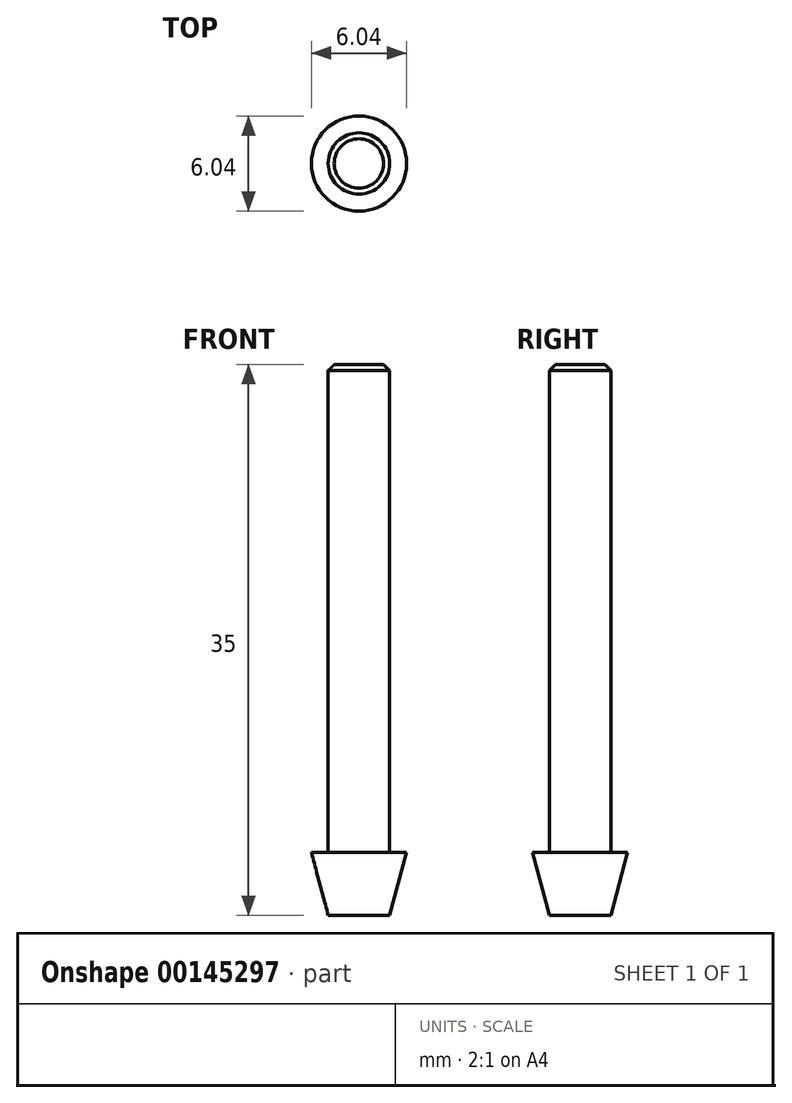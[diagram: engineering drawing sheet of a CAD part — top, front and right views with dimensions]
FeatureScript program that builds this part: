
annotation { "Feature Type Name" : "Feature", "Feature Type Description" : "" }
export const myFeature = defineFeature(function(context is Context, id is Id, definition is map)
    precondition{}
    {
        {
            var Q0;
            Q0=qCreatedBy(makeId("Front.planeOp"),FACE);
            var sketch = newSketch(context, id + "F0", { "sketchPlane" : qUnion([Q0])});
            skLineSegment(sketch, "E0", {"start": v(0, 0) * mm, "end": v(0, 35) * mm});
            skLineSegment(sketch, "E1", {"start": v(0, 0) * mm, "end": v(1.95, 0) * mm});
            skLineSegment(sketch, "E2.0", {"start": v(1.95, 4) * mm, "end": v(3.02, 4) * mm});
            skLineSegment(sketch, "E3", {"start": v(1.95, 0) * mm, "end": v(3.02, 4) * mm});
            skLineSegment(sketch, "E4.0", {"start": v(1.95, 4) * mm, "end": v(1.95, 35) * mm});
            skLineSegment(sketch, "E5", {"start": v(0, 35) * mm, "end": v(1.95, 35) * mm});
            skSolve(sketch);
        }
        {
            var Q0;
            Q0 = qSketchRegion(id + "F0", true);
            var Q1;
            Q1=sQuery(id+"F0.wireOp",EDGE,"E0");
            revolve(context, id + "F1", {"entities" : qUnion([Q0]), "axis" : qUnion([Q1]), "revolveType" : RevolveType.FULL});
        }
        {
            var Q0;
            Q0=makeQuery(id+"F1.opRevolve","SWEPT_EDGE",EDGE,{"disambiguationData":[OSD([sQuery(id+"F0.wireOp",EDGE,"E4.0"),sQuery(id+"F0.wireOp",EDGE,"E5")])]});
            chamfer(context, id + "F2", {"entities" : qUnion([Q0]), "width" : 0.38 * mm, "tangentPropagation" : true});
        }
    });
